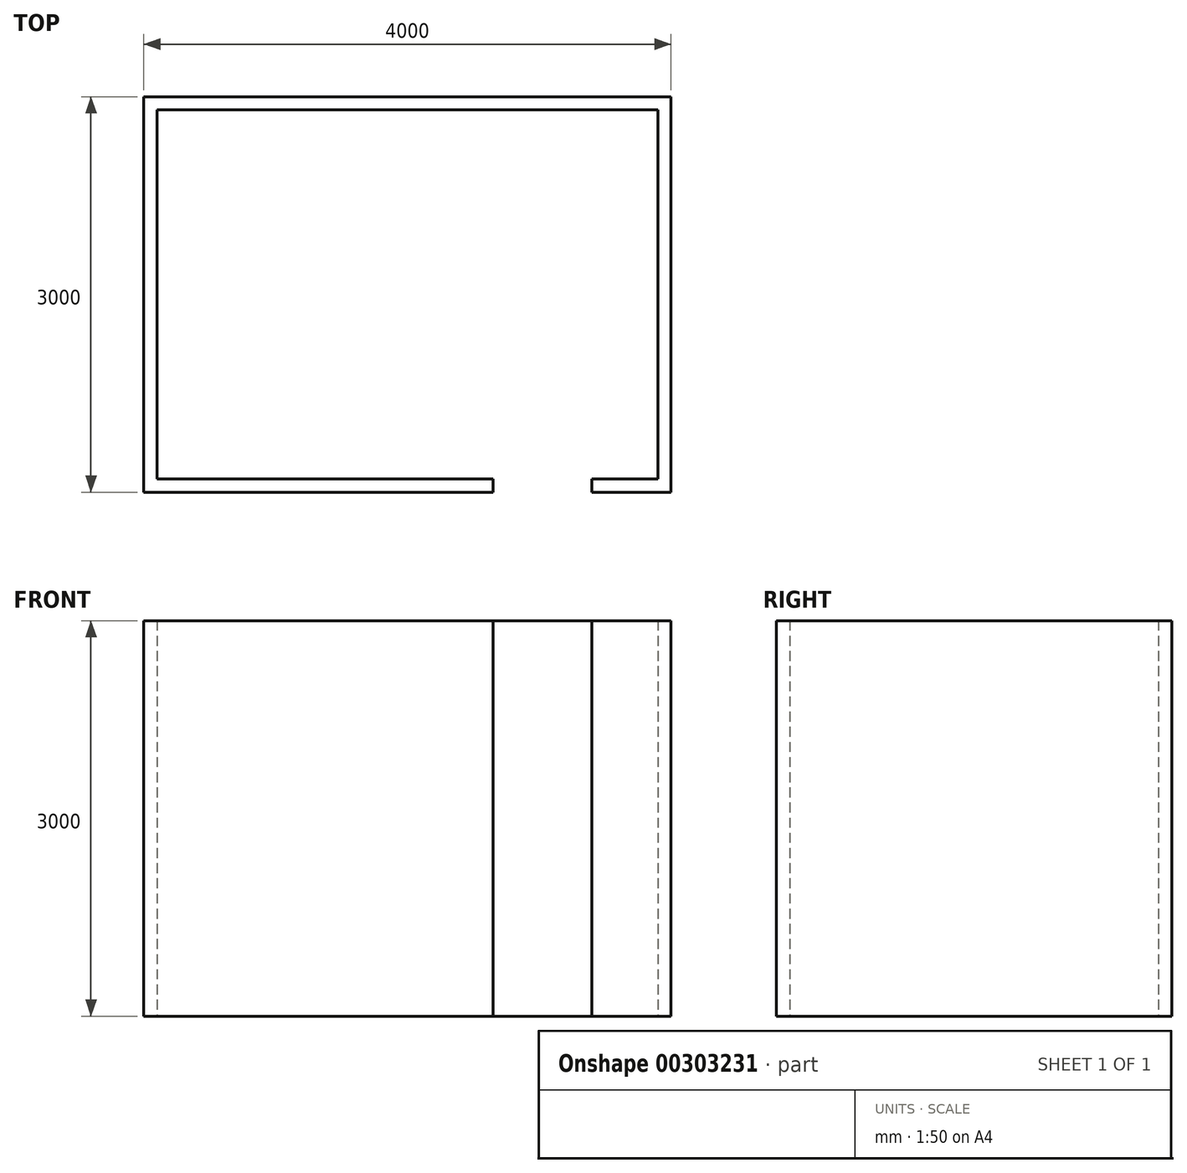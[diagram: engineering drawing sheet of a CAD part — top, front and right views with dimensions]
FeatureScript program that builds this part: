
annotation { "Feature Type Name" : "Feature", "Feature Type Description" : "" }
export const myFeature = defineFeature(function(context is Context, id is Id, definition is map)
    precondition{}
    {
        {
            var Q0;
            Q0=qCreatedBy(makeId("Top.planeOp"),FACE);
            var sketch = newSketch(context, id + "F0", { "sketchPlane" : qUnion([Q0])});
            skLineSegment(sketch, "E0.bottom", {"start": v(-1998.48, 1777.57) * mm, "end": v(2001.52, 1777.57) * mm});
            skLineSegment(sketch, "E0.left", {"start": v(-1998.48, 1777.57) * mm, "end": v(-1998.48, -1222.43) * mm});
            skLineSegment(sketch, "E0.right", {"start": v(2001.52, 1777.57) * mm, "end": v(2001.52, -1222.43) * mm});
            skLineSegment(sketch, "E1", {"start": v(-1898.48, 1677.57) * mm, "end": v(-1898.48, -1122.43) * mm});
            skLineSegment(sketch, "E2", {"start": v(1901.52, -1122.43) * mm, "end": v(1901.52, 1677.57) * mm});
            skLineSegment(sketch, "E3", {"start": v(-1898.48, 1677.57) * mm, "end": v(1901.52, 1677.57) * mm});
            skLineSegment(sketch, "E4", {"start": v(2001.52, -1222.43) * mm, "end": v(1401.52, -1222.43) * mm});
            skPoint(sketch, "E5.end.orphan", {"position": v(1401.52, -1122.43) * mm});
            skPoint(sketch, "E5.start.orphan", {"position": v(651.52, -1122.43) * mm});
            skLineSegment(sketch, "E6", {"start": v(651.52, -1122.43) * mm, "end": v(-1898.48, -1122.43) * mm});
            skLineSegment(sketch, "E7", {"start": v(1401.52, -1122.43) * mm, "end": v(1901.52, -1122.43) * mm});
            skLineSegment(sketch, "E8", {"start": v(1401.52, -1222.43) * mm, "end": v(1401.52, -1122.43) * mm});
            skLineSegment(sketch, "E9", {"start": v(651.52, -1222.43) * mm, "end": v(651.52, -1122.43) * mm});
            skLineSegment(sketch, "E10", {"start": v(-1998.48, -1222.43) * mm, "end": v(651.52, -1222.43) * mm});
            skLineSegment(sketch, "E11", {"start": v(-1898.48, 774.25) * mm, "end": v(-1998.48, 774.25) * mm});
            skSolve(sketch);
        }
        {
            var Q0;
            {var subQ4=sQuery(id+"F0.wireOp",EDGE,"E0.bottom");Q0=makeQuery(id+"F0.imprint","IMPRINT",FACE,{"disambiguationData":[TD([[makeQuery(id+"F0.imprint","IMPRINT",EDGE,{"derivedFrom":subQ4}),-1.0]])]});}
            var Q1;
            {var subQ0=sQuery(id+"F0.wireOp",EDGE,"E6");Q1=makeQuery(id+"F0.imprint","IMPRINT",FACE,{"disambiguationData":[TD([[makeQuery(id+"F0.imprint","IMPRINT",EDGE,{"derivedFrom":subQ0}),1.0]])]});}
            extrude(context, id + "F1", {"entities" : qUnion([Q0, Q1]), "depth" : 3000 * mm});
        }
    });
